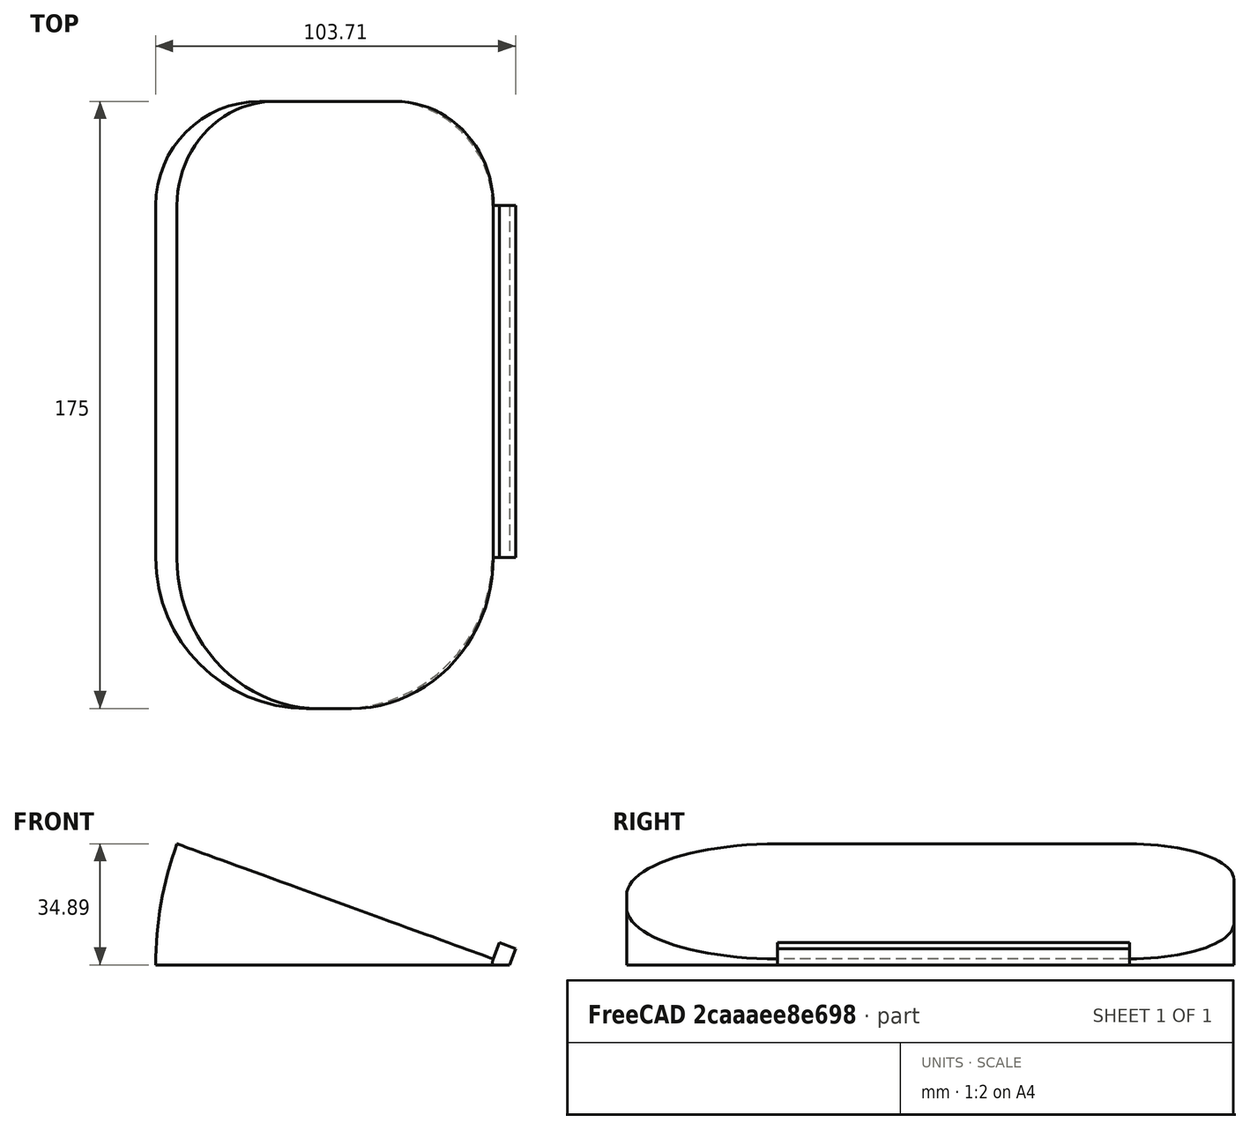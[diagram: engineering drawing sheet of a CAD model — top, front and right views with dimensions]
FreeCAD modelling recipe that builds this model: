
FCSTD DOCUMENT  (FreeCAD 0.19R24291 (Git))
Label: trackman-wedge
License: All rights reserved
LicenseURL: http://en.wikipedia.org/wiki/All_rights_reserved
objects: Sketcher::SketchObject×2, PartDesign::Revolution×1, PartDesign::Pad×1, PartDesign::Body×1, Mesh::Feature×1
note: 7 computed .brp shape members not serialized (recipe doc carries the construction recipe); baked Part::Feature solids carry a one-line shape summary decoded from their .brp

FEATURE [Sketcher::SketchObject] Sketch
  FullyConstrained = true
  MapMode = 5
  Support = -> [XY_Plane]
  sketch-geometry (28):
    g0: GeomPoint X=-48.5 Y=87.5 Z=0
    g1: GeomPoint X=48.5 Y=87.5 Z=0
    g2: GeomPoint X=-48.5 Y=-87.5 Z=0
    g3: GeomPoint X=48.5 Y=-87.5 Z=0
    g4: LineSegment StartX=-18.5 StartY=87.5 StartZ=0 EndX=18.5 EndY=87.5 EndZ=0
    g5: LineSegment StartX=-48.5 StartY=57.5 StartZ=0 EndX=-48.5 EndY=-44 EndZ=0
    g6: LineSegment StartX=-5 StartY=-87.5 StartZ=0 EndX=5 EndY=-87.5 EndZ=0
    g7: ArcOfCircle CenterX=-18.5 CenterY=57.5 CenterZ=0 NormalX=0 NormalY=0 NormalZ=1 AngleXU=0 Radius=30 StartAngle=1.5708 EndAngle=3.14159
    g8: GeomPoint X=-48.5 Y=87.5 Z=0
    g9: ArcOfCircle CenterX=18.5 CenterY=57.5 CenterZ=0 NormalX=0 NormalY=0 NormalZ=1 AngleXU=0 Radius=30 StartAngle=0 EndAngle=1.5708
    g10: GeomPoint X=48.5 Y=87.5 Z=0
    g11: ArcOfCircle CenterX=5 CenterY=-44 CenterZ=0 NormalX=0 NormalY=0 NormalZ=1 AngleXU=0 Radius=43.5 StartAngle=4.71239 EndAngle=6.28319
    g12: GeomPoint X=48.5 Y=-87.5 Z=0
    g13: ArcOfCircle CenterX=-5 CenterY=-44 CenterZ=0 NormalX=0 NormalY=0 NormalZ=1 AngleXU=0 Radius=43.5 StartAngle=3.14159 EndAngle=4.71239
    g14: GeomPoint X=-48.5 Y=-87.5 Z=0
    g15: LineSegment StartX=-48.5 StartY=57.5 StartZ=0 EndX=-18.5 EndY=57.5 EndZ=0
    g16: LineSegment StartX=18.5 StartY=57.5 StartZ=0 EndX=48.5 EndY=57.5 EndZ=0
    g17: LineSegment StartX=-5 StartY=-44 StartZ=0 EndX=5 EndY=-44 EndZ=0
    g18: LineSegment StartX=48.5 StartY=57.5 StartZ=0 EndX=48.5 EndY=-44 EndZ=0
    g19: LineSegment StartX=18.5 StartY=87.5 StartZ=0 EndX=18.5 EndY=57.5 EndZ=0
    g20: LineSegment StartX=48.5 StartY=-87.5 StartZ=0 EndX=48.5 EndY=-44 EndZ=0
    g21: LineSegment StartX=48.5 StartY=57.5 StartZ=0 EndX=48.5 EndY=87.5 EndZ=0
    g22: LineSegment StartX=48.5 StartY=-44 StartZ=0 EndX=5 EndY=-44 EndZ=0
    g23: LineSegment StartX=5 StartY=-44 StartZ=0 EndX=5 EndY=-87.5 EndZ=0
    g24: LineSegment StartX=48.5 StartY=57.5 StartZ=0 EndX=53.5 EndY=57.5 EndZ=0
    g25: LineSegment StartX=53.5 StartY=57.5 StartZ=0 EndX=53.5 EndY=-44 EndZ=0
    g26: LineSegment StartX=53.5 StartY=-44 StartZ=0 EndX=48.5 EndY=-44 EndZ=0
    g27: LineSegment StartX=53.5 StartY=57.5 StartZ=0 EndX=53.5 EndY=-44 EndZ=0
  constraints (59):
    c: DistanceY(g2,g0) = 175
    c: DistanceX(g0,g1) = 97
    c: Symmetric(g0,g3,g-1)
    c: Coincident(g8,g0)
    c: Coincident(g10,g1)
    c: Horizontal(g4)
    c: Coincident(g14,g2)
    c: Vertical(g5)
    c: Coincident(g12,g3)
    c: Horizontal(g6)
    c: PointOnObject(g8,g5)
    c: PointOnObject(g8,g4)
    c: Tangent(g5,g7) = -1.5708
    c: Tangent(g4,g7) = 1.5708
    c: PointOnObject(g10,g4)
    c: Tangent(g4,g9) = 1.5708
    c: Coincident(g16,g9) = 1.5708
    c: PointOnObject(g12,g6)
    c: Coincident(g18,g11) = 1.5708
    c: Tangent(g6,g11) = -1.5708
    c: PointOnObject(g14,g5)
    c: PointOnObject(g14,g6)
    c: Tangent(g5,g13) = -1.5708
    c: Tangent(g6,g13) = -1.5708
    c: Coincident(g15,g5)
    c: Coincident(g15,g7)
    c: Coincident(g16,g9)
    c: Equal(g15,g16)
    c: DistanceX(g15,g15) = 30
    c: Coincident(g17,g13)
    c: Horizontal(g17)
    c: Coincident(g11,g17)
    c: DistanceX(g17,g17) = 10
    c: Coincident(g18,g9)
    c: Coincident(g19,g4)
    c: Coincident(g19,g9)
    c: Angle(g16,g19) = 1.5708
    c: Vertical(g18)
    c: Coincident(g20,g11)
    c: Vertical(g20)
    c: Coincident(g3,g20)
    c: Coincident(g21,g9)
    c: Coincident(g21,g1)
    c: Vertical(g21)
    c: Coincident(g22,g11)
    c: Coincident(g22,g11)
    c: Coincident(g23,g11)
    c: Coincident(g23,g6)
    c: Horizontal(g22)
    c: Horizontal(g24)
    c: Coincident(g24,g25)
    c: Vertical(g25)
    c: Coincident(g25,g26)
    c: Coincident(g26,g11)
    c: Horizontal(g26)
    c: DistanceX(g24,g24) = 5
    c: Coincident(g9,g24)
    c: Coincident(g27,g24)
    c: Coincident(g27,g25)
FEATURE [PartDesign::Revolution] Revolution
  Angle = 20
  Axis = (0,-101.5,0)
  Base = (53.5,57.5,0)
  Profile = -> Sketch
  ReferenceAxis = -> Sketch [Axis9]
  Refine = true
  Reversed = true
FEATURE [Sketcher::SketchObject] Sketch001
  ExternalGeometry = -> [Revolution]
  FullyConstrained = true
  MapMode = 5
  Placement = pos=(6.25831,0,17.1946) rot=(0,1,0;0.349066rad)
  Support = -> [Revolution]
  sketch-geometry (4):
    g0: LineSegment StartX=45.2736 StartY=-44 StartZ=0 EndX=50.2736 EndY=-44 EndZ=0
    g1: LineSegment StartX=50.2736 StartY=-44 StartZ=0 EndX=50.2736 EndY=57.5 EndZ=0
    g2: LineSegment StartX=50.2736 StartY=57.5 StartZ=0 EndX=45.2736 EndY=57.5 EndZ=0
    g3: LineSegment StartX=45.2736 StartY=57.5 StartZ=0 EndX=45.2736 EndY=-44 EndZ=0
  constraints (10):
    c: Coincident(g0,g1)
    c: Coincident(g1,g2)
    c: Coincident(g2,g3)
    c: Coincident(g3,g0)
    c: Horizontal(g0)
    c: Horizontal(g2)
    c: Vertical(g1)
    c: Vertical(g3)
    c: Coincident(g0,g-4)
    c: Coincident(g1,g-3)
FEATURE [PartDesign::Pad] Pad
  BaseFeature = -> Revolution
  Direction = (1,1,1)
  Length = 5
  Length2 = 100
  Profile = -> Sketch001
  Refine = true
  Type = 0
FEATURE [PartDesign::Body] Body
  Group = -> [Sketch,Revolution,Sketch001,Pad]
  Origin = -> Origin
  Tip = -> Pad
FEATURE [Mesh::Feature] Mesh  label="Body (Meshed)"
